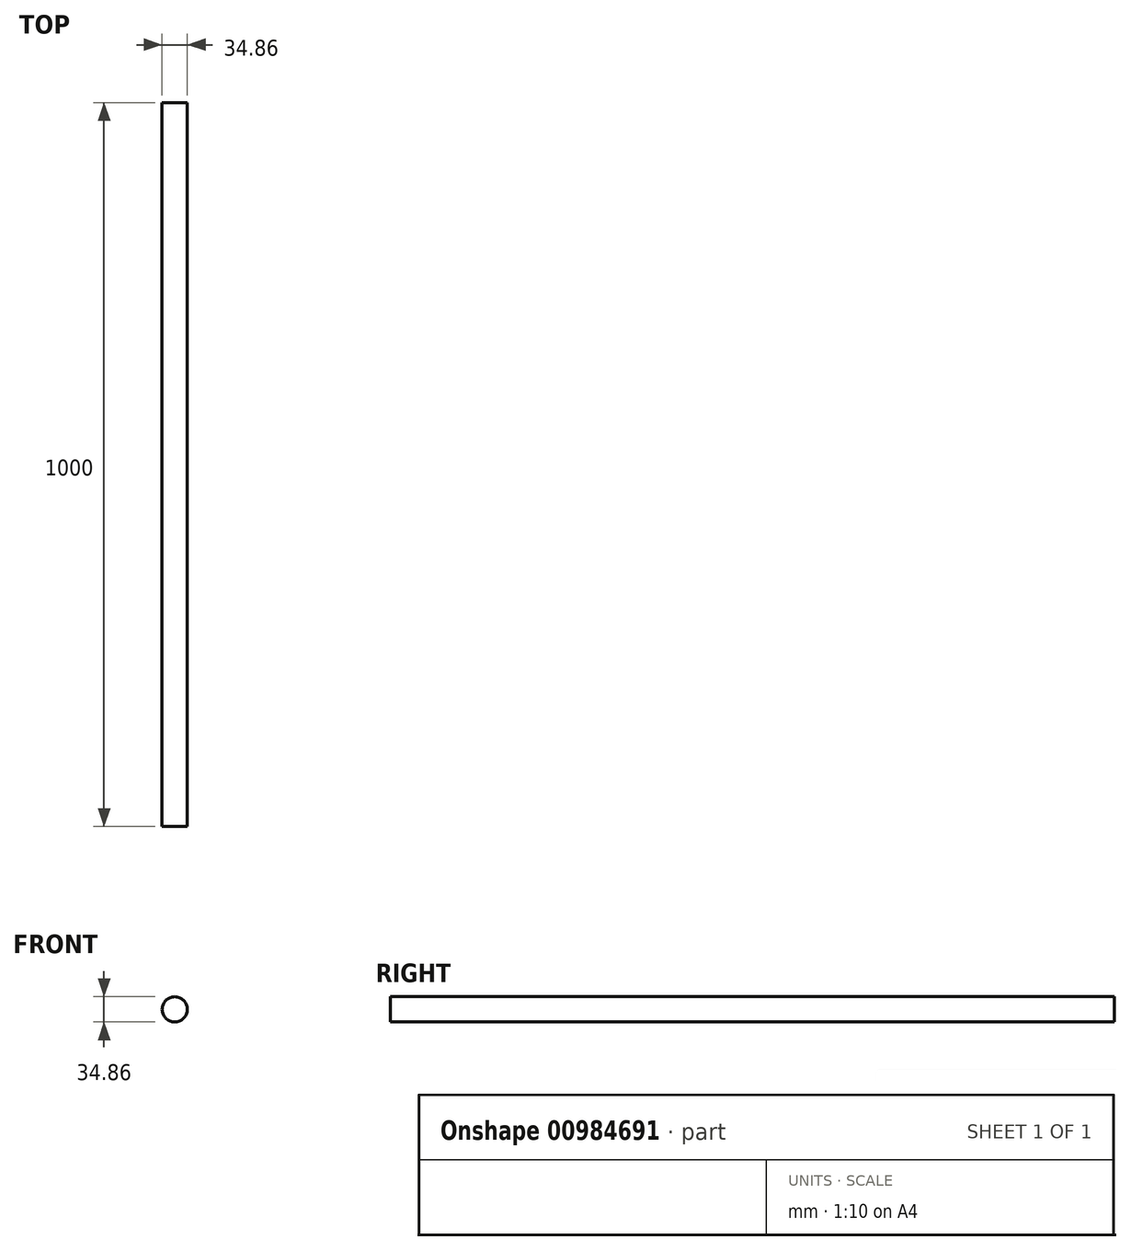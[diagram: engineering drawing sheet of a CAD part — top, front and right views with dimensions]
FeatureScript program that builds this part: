
annotation { "Feature Type Name" : "Feature", "Feature Type Description" : "" }
export const myFeature = defineFeature(function(context is Context, id is Id, definition is map)
    precondition{}
    {
        {
            var Q0;
            Q0=qCreatedBy(makeId("Front.planeOp"),FACE);
            var sketch = newSketch(context, id + "F0", { "sketchPlane" : qUnion([Q0])});
            skCircle(sketch, "E0", {"center": v(0, 0) * mm, "radius": 17.43 * mm});
            skSolve(sketch);
        }
        {
            var Q0;
            Q0=makeQuery(id+"F0.imprint","IMPRINT",FACE,{"disambiguationData":[TD([[makeQuery(id+"F0.imprint","IMPRINT",EDGE,{"derivedFrom":sQuery(id+"F0.wireOp",EDGE,"E0")}),1.0]])]});
            extrude(context, id + "F1", {"entities" : qUnion([Q0]), "oppositeDirection" : true, "depth" : 1000 * mm, "offsetDistance" : 25 * mm});
        }
    });
